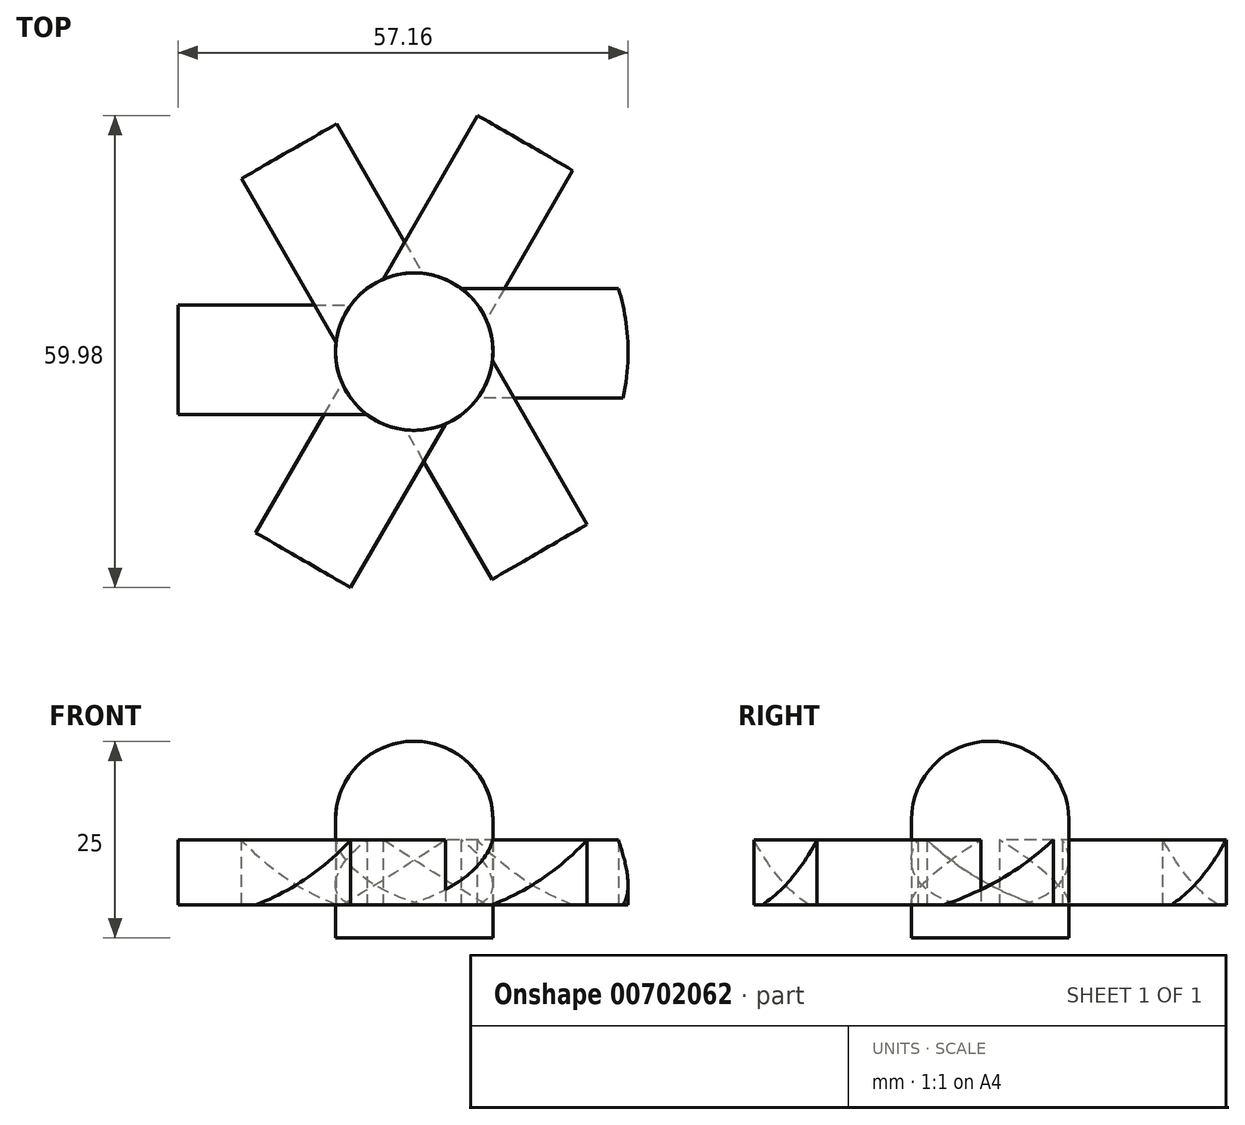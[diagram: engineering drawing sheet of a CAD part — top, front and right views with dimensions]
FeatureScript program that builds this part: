
annotation { "Feature Type Name" : "Feature", "Feature Type Description" : "" }
export const myFeature = defineFeature(function(context is Context, id is Id, definition is map)
    precondition{}
    {
        {
            var Q0;
            Q0=qCreatedBy(makeId("Top.planeOp"),FACE);
            var sketch = newSketch(context, id + "F0", { "sketchPlane" : qUnion([Q0])});
            skCircle(sketch, "E0", {"center": v(0, 0) * mm, "radius": 10 * mm});
            skSolve(sketch);
        }
        {
            var Q0;
            Q0=makeQuery(id+"F0.imprint","IMPRINT",FACE,{"disambiguationData":[TD([[makeQuery(id+"F0.imprint","IMPRINT",EDGE,{"derivedFrom":sQuery(id+"F0.wireOp",EDGE,"E0")}),1.0]])]});
            extrude(context, id + "F1", {"entities" : qUnion([Q0]), "depth" : 25 * mm, "offsetDistance" : 25 * mm});
        }
        {
            var Q0;
            Q0=makeQuery(id+"F1.opExtrude","CAP_FACE",FACE,{"disambiguationData":[OSD([sQuery(id+"F0.wireOp",EDGE,"E0")])],"isStart":false});
            fillet(context, id + "F2", {"entities" : qUnion([Q0]), "radius" : 10 * mm, "tangentPropagation" : true, "allowEdgeOverflow" : false});
        }
        {
            var Q0;
            Q0=qCreatedBy(makeId("Right.planeOp"),FACE);
            var sketch = newSketch(context, id + "F3", { "sketchPlane" : qUnion([Q0])});
            skLineSegment(sketch, "E1", {"start": v(-5.91, 4.22) * mm, "end": v(8.02, 4.22) * mm});
            skLineSegment(sketch, "E2", {"start": v(8.02, 4.22) * mm, "end": v(8.02, 12.44) * mm});
            skArc(sketch, "E3", {"start": v(-5.91, 4.22) * mm, "mid": v(1.5, 7.57) * mm, "end": v(8.02, 12.44) * mm});
            skSolve(sketch);
        }
        {
            var Q0;
            Q0 = qSketchRegion(id + "F3", true);
            extrude(context, id + "F4", {"entities" : qUnion([Q0]), "operationType" : NewBodyOperationType.ADD, "depth" : 30 * mm, "offsetDistance" : 25 * mm});
        }
        {
            var Q0;
            Q0=qCreatedBy(makeId("Right.planeOp"),FACE);
            var sketch = newSketch(context, id + "F5", { "sketchPlane" : qUnion([Q0])});
            skLineSegment(sketch, "E4", {"start": v(0, 0) * mm, "end": v(0, 38.58) * mm});
            skSolve(sketch);
        }
        {
            var Q0;
            Q0=makeQuery(id+"F1.opExtrude","SWEPT_BODY",BODY,{"disambiguationData":[OSD([sQuery(id+"F0.wireOp",EDGE,"E0")])]});
            var Q1;
            Q1=sQuery(id+"F5.wireOp",EDGE,"E4");
            circularPattern(context, id + "F6", {"entities" : qUnion([Q0]), "axis" : qUnion([Q1]), "angle" : 360 * degree, "instanceCount" : 6, "equalSpace" : true});
        }
        {
            var Q0;
            Q0=makeQuery(id+"F1.opExtrude","CAP_FACE",FACE,{"disambiguationData":[OSD([sQuery(id+"F0.wireOp",EDGE,"E0")])],"isStart":true});
            var sketch = newSketch(context, id + "F7", { "sketchPlane" : qUnion([Q0])});
            skCircle(sketch, "E5", {"center": v(0, 0) * mm, "radius": 27.16 * mm});
            skSolve(sketch);
        }
        {
            var Q0;
            Q0 = qSketchRegion(id + "F7", true);
            extrude(context, id + "F8", {"entities" : qUnion([Q0]), "oppositeDirection" : true, "depth" : 35.2 * mm, "offsetDistance" : 25 * mm});
        }
        {
            var Q0;
            Q0=makeQuery(id+"F8.opExtrude","SWEPT_BODY",BODY,{"disambiguationData":[OSD([sQuery(id+"F7.wireOp",EDGE,"E5")])]});
            var Q1;
            Q1=makeQuery(id+"F1.opExtrude","SWEPT_BODY",BODY,{"disambiguationData":[OSD([sQuery(id+"F0.wireOp",EDGE,"E0")])]});
            booleanBodies(context, id + "F9", {"operationType" : BooleanOperationType.INTERSECTION, "tools" : qUnion([Q0, Q1])});
        }
    });
